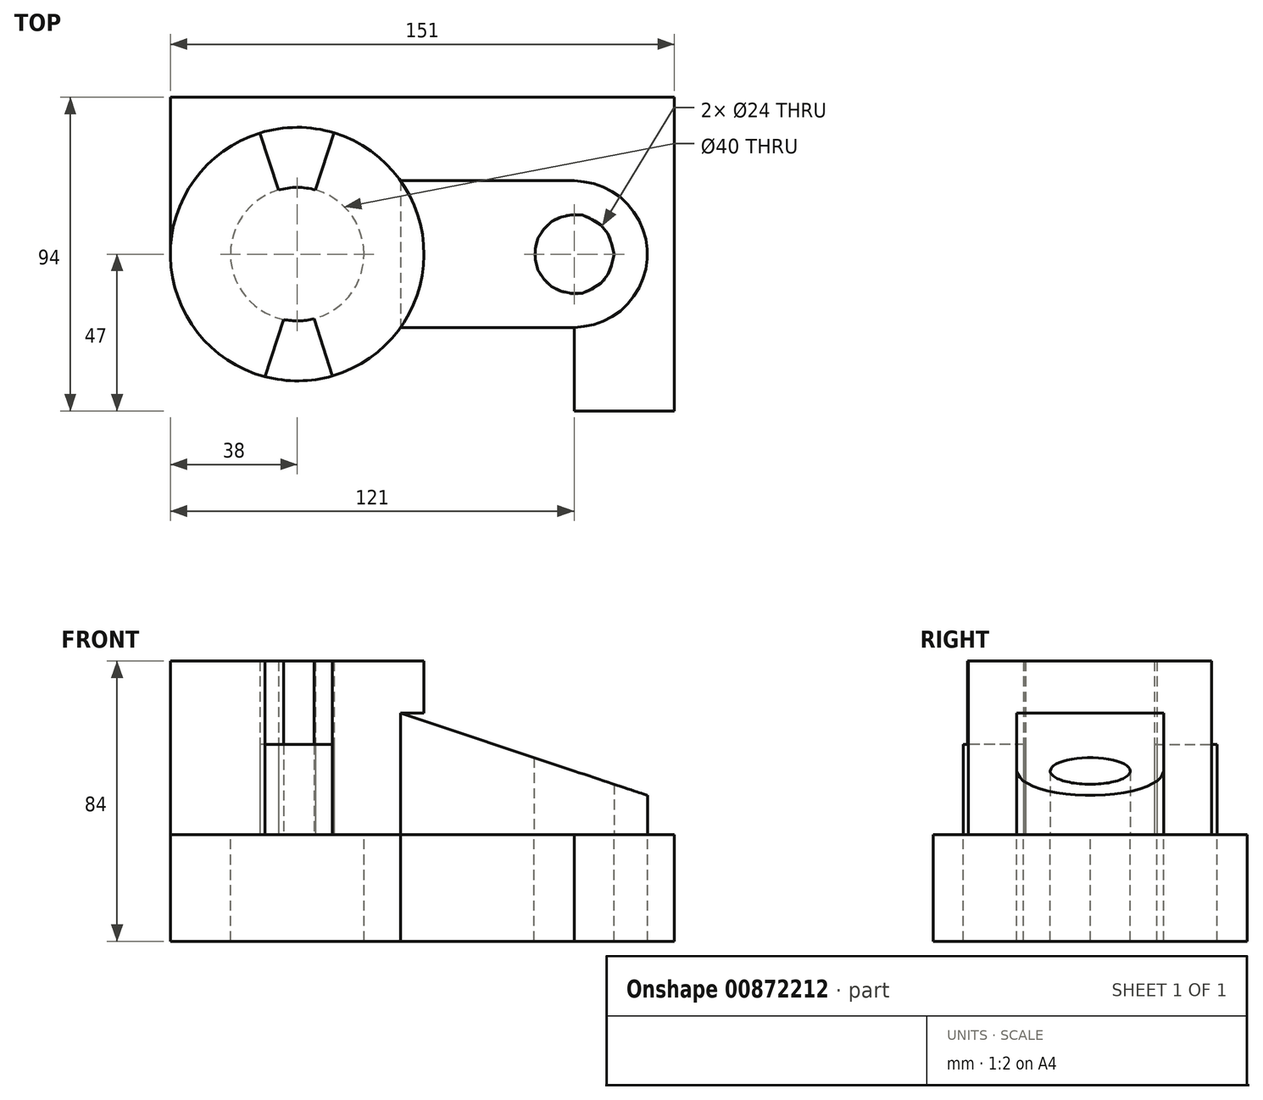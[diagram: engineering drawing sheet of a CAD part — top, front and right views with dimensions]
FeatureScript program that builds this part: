
annotation { "Feature Type Name" : "Feature", "Feature Type Description" : "" }
export const myFeature = defineFeature(function(context is Context, id is Id, definition is map)
    precondition{}
    {
        {
            var Q0;
            Q0=qCreatedBy(makeId("Top.planeOp"),FACE);
            var sketch = newSketch(context, id + "F0", { "sketchPlane" : qUnion([Q0])});
            skLineSegment(sketch, "E0.bottom", {"start": v(-56.5, 47) * mm, "end": v(56.5, 47) * mm});
            skLineSegment(sketch, "E0.top", {"start": v(-56.5, -47) * mm, "end": v(56.5, -47) * mm});
            skLineSegment(sketch, "E0.right", {"start": v(56.5, 47) * mm, "end": v(56.5, -47) * mm});
            skPoint(sketch, "E0.middle", {"position": v(0, 0) * mm});
            skCircle(sketch, "E1", {"center": v(-56.5, 0) * mm, "radius": 38 * mm});
            skLineSegment(sketch, "E2", {"start": v(-94.5, -47) * mm, "end": v(-56.5, -47) * mm});
            skLineSegment(sketch, "E3", {"start": v(-94.5, 47) * mm, "end": v(-56.5, 47) * mm});
            skLineSegment(sketch, "E4", {"start": v(56.5, -47) * mm, "end": v(26.5, -47) * mm});
            skLineSegment(sketch, "E5", {"start": v(26.5, -47) * mm, "end": v(26.5, 47) * mm});
            skCircle(sketch, "E6", {"center": v(26.5, 0) * mm, "radius": 12 * mm});
            skArc(sketch, "E7", {"start": v(26.5, -22) * mm, "mid": v(48.5, 0) * mm, "end": v(26.5, 22) * mm});
            skLineSegment(sketch, "E8", {"start": v(26.5, 22) * mm, "end": v(-25.52, 22) * mm});
            skLineSegment(sketch, "E9", {"start": v(26.5, -22) * mm, "end": v(-25.52, -22) * mm});
            skCircle(sketch, "E10", {"center": v(-56.5, 0) * mm, "radius": 20 * mm});
            skLineSegment(sketch, "E11", {"start": v(-51.48, -19.36) * mm, "end": v(-45.91, -36.5) * mm});
            skLineSegment(sketch, "E12", {"start": v(-56.5, 0) * mm, "end": v(-56.5, 38) * mm});
            skLineSegment(sketch, "E13", {"start": v(-56.5, 0) * mm, "end": v(-56.5, -38) * mm});
            skLineSegment(sketch, "E14", {"start": v(-51, 19.23) * mm, "end": v(-45.43, 36.35) * mm});
            skLineSegment(sketch, "E15", {"start": v(-62.12, 19.2) * mm, "end": v(-67.69, 36.32) * mm});
            skPoint(sketch, "E16.startSnap0", {"position": v(-56.5, -19) * mm});
            skLineSegment(sketch, "E17", {"start": v(-60.62, -19.57) * mm, "end": v(-66.2, -36.74) * mm});
            skLineSegment(sketch, "E18", {"start": v(-94.5, -47) * mm, "end": v(-94.5, 47) * mm});
            skSolve(sketch);
        }
        {
            var Q0;
            {var subQ0=sQuery(id+"F0.wireOp",EDGE,"E15");Q0=makeQuery(id+"F0.imprint","IMPRINT",FACE,{"disambiguationData":[TD([[makeQuery(id+"F0.imprint","IMPRINT",EDGE,{"derivedFrom":subQ0}),1.0]])]});}
            var Q1;
            {var subQ0=sQuery(id+"F0.wireOp",EDGE,"E11");Q1=makeQuery(id+"F0.imprint","IMPRINT",FACE,{"disambiguationData":[TD([[makeQuery(id+"F0.imprint","IMPRINT",EDGE,{"derivedFrom":subQ0}),1.0]])]});}
            var Q2;
            {var subQ3=sQuery(id+"F0.wireOp",EDGE,"E10");var subQ7=makeQuery(id+"F0.imprint","INTERSECT",VERTEX,{"derivedFrom":[subQ3,sQuery(id+"F0.wireOp",EDGE,"E14")]});Q2=makeQuery(id+"F0.imprint","IMPRINT",FACE,{"disambiguationData":[TD([[makeQuery(id+"F0.imprint","IMPRINT",EDGE,{"disambiguationData":[TD([[subQ7,-1.0]])],"derivedFrom":subQ3}),1.0]])]});}
            var Q3;
            {var subQ0=sQuery(id+"F0.wireOp",EDGE,"E10");var subQ7=makeQuery(id+"F0.imprint","INTERSECT",VERTEX,{"derivedFrom":[subQ0,sQuery(id+"F0.wireOp",EDGE,"E15")]});Q3=makeQuery(id+"F0.imprint","IMPRINT",FACE,{"disambiguationData":[TD([[makeQuery(id+"F0.imprint","IMPRINT",EDGE,{"disambiguationData":[TD([[subQ7,1.0]])],"derivedFrom":subQ0}),1.0]])]});}
            extrude(context, id + "F1", {"entities" : qUnion([Q0, Q1, Q2, Q3]), "depth" : (84 - 32) * mm, "offsetDistance" : 25 * mm});
        }
        {
            var Q0;
            {var subQ0=sQuery(id+"F0.wireOp",EDGE,"E11");Q0=makeQuery(id+"F0.imprint","IMPRINT",FACE,{"disambiguationData":[TD([[makeQuery(id+"F0.imprint","IMPRINT",EDGE,{"derivedFrom":subQ0}),-1.0]])]});}
            var Q1;
            {var subQ3=sQuery(id+"F0.wireOp",EDGE,"E17");Q1=makeQuery(id+"F0.imprint","IMPRINT",FACE,{"disambiguationData":[TD([[makeQuery(id+"F0.imprint","IMPRINT",EDGE,{"derivedFrom":subQ3}),1.0]])]});}
            var Q2;
            {var subQ3=sQuery(id+"F0.wireOp",EDGE,"E14");Q2=makeQuery(id+"F0.imprint","IMPRINT",FACE,{"disambiguationData":[TD([[makeQuery(id+"F0.imprint","IMPRINT",EDGE,{"derivedFrom":subQ3}),1.0]])]});}
            var Q3;
            {var subQ3=sQuery(id+"F0.wireOp",EDGE,"E15");Q3=makeQuery(id+"F0.imprint","IMPRINT",FACE,{"disambiguationData":[TD([[makeQuery(id+"F0.imprint","IMPRINT",EDGE,{"derivedFrom":subQ3}),-1.0]])]});}
            extrude(context, id + "F2", {"entities" : qUnion([Q0, Q1, Q2, Q3]), "depth" : (52 - 25) * mm, "offsetDistance" : 25 * mm});
        }
        {
            var Q0;
            {var subQ5=sQuery(id+"F0.wireOp",EDGE,"E3");Q0=makeQuery(id+"F0.imprint","IMPRINT",FACE,{"disambiguationData":[TD([[makeQuery(id+"F0.imprint","IMPRINT",EDGE,{"derivedFrom":subQ5}),-1.0]])]});}
            var Q1;
            {var subQ6=sQuery(id+"F0.wireOp",EDGE,"E0.top");Q1=makeQuery(id+"F0.imprint","IMPRINT",FACE,{"disambiguationData":[TD([[makeQuery(id+"F0.imprint","IMPRINT",EDGE,{"derivedFrom":subQ6}),1.0]])]});}
            extrude(context, id + "F3", {"entities" : qUnion([Q0, Q1]), "oppositeDirection" : true, "depth" : 32 * mm, "offsetDistance" : 25 * mm});
        }
        {
            var Q0;
            {var subQ1=sQuery(id+"F0.wireOp",EDGE,"E0.right");Q0=makeQuery(id+"F0.imprint","IMPRINT",FACE,{"disambiguationData":[TD([[makeQuery(id+"F0.imprint","IMPRINT",EDGE,{"derivedFrom":subQ1}),-1.0]])]});}
            extrude(context, id + "F4", {"entities" : qUnion([Q0]), "oppositeDirection" : true, "depth" : 32 * mm, "offsetDistance" : 25 * mm});
        }
        {
            var Q0;
            {var subQ4=sQuery(id+"F0.wireOp",EDGE,"E8");Q0=makeQuery(id+"F0.imprint","IMPRINT",FACE,{"disambiguationData":[TD([[makeQuery(id+"F0.imprint","IMPRINT",EDGE,{"derivedFrom":subQ4}),1.0]])]});}
            var Q1;
            {var subQ0=sQuery(id+"F0.wireOp",EDGE,"E7");Q1=makeQuery(id+"F0.imprint","IMPRINT",FACE,{"disambiguationData":[TD([[makeQuery(id+"F0.imprint","IMPRINT",EDGE,{"derivedFrom":subQ0}),1.0]])]});}
            extrude(context, id + "F5", {"entities" : qUnion([Q0, Q1]), "operationType" : NewBodyOperationType.ADD, "depth" : 12 * mm, "offsetDistance" : 25 * mm});
        }
        {
            var Q0;
            Q0=makeQuery(id+"F5.opExtrude","CAP_FACE",FACE,{"disambiguationData":[OSD([sQuery(id+"F0.wireOp",EDGE,"E1"),sQuery(id+"F0.wireOp",EDGE,"E6"),sQuery(id+"F0.wireOp",EDGE,"E7"),sQuery(id+"F0.wireOp",EDGE,"E8"),sQuery(id+"F0.wireOp",EDGE,"E9")])],"isStart":false});
            extrude(context, id + "F6", {"entities" : qUnion([Q0]), "operationType" : NewBodyOperationType.ADD, "depth" : 24.4 * mm, "offsetDistance" : 25 * mm});
        }
        {
            var Q0;
            {var subQ0=sQuery(id+"F0.wireOp",EDGE,"E9");Q0=makeQuery(id+"F6.boolean.opBoolean","MERGE",FACE,{"derivedFrom":[makeQuery(id+"F5.opExtrude","SWEPT_FACE",FACE,{"disambiguationData":[OSD([subQ0])]}),makeQuery(id+"F6.opExtrude","SWEPT_FACE",FACE,{"disambiguationData":[OSD([subQ0])]})]});}
            var sketch = newSketch(context, id + "F7", { "sketchPlane" : qUnion([Q0])});
            skLineSegment(sketch, "E19", {"start": v(48.5, 36.4) * mm, "end": v(48.5, 0) * mm});
            skLineSegment(sketch, "E20.0.0", {"start": v(-25.52, 0) * mm, "end": v(26.5, 0) * mm});
            skLineSegment(sketch, "E20.0.1", {"start": v(26.5, 0) * mm, "end": v(26.5, 36.4) * mm});
            skLineSegment(sketch, "E20.0.2", {"start": v(26.5, 36.4) * mm, "end": v(-25.52, 36.4) * mm});
            skLineSegment(sketch, "E20.0.3", {"start": v(-25.52, 36.4) * mm, "end": v(-25.52, 0) * mm});
            skLineSegment(sketch, "E21", {"start": v(-25.52, 36.4) * mm, "end": v(48.5, 11.72) * mm});
            skLineSegment(sketch, "E22", {"start": v(26.5, 36.4) * mm, "end": v(48.5, 36.4) * mm});
            skSolve(sketch);
        }
        {
            var Q0;
            {var subQ0=sQuery(id+"F7.wireOp",EDGE,"E20.0.2");Q0=makeQuery(id+"F7.imprint","IMPRINT",FACE,{"disambiguationData":[TD([[makeQuery(id+"F7.imprint","IMPRINT",EDGE,{"derivedFrom":subQ0}),1.0]])]});}
            var Q1;
            {var subQ0=sQuery(id+"F7.wireOp",EDGE,"E22");Q1=makeQuery(id+"F7.imprint","IMPRINT",FACE,{"disambiguationData":[TD([[makeQuery(id+"F7.imprint","IMPRINT",EDGE,{"derivedFrom":subQ0}),-1.0]])]});}
            extrude(context, id + "F8", {"entities" : qUnion([Q0, Q1]), "operationType" : NewBodyOperationType.REMOVE, "oppositeDirection" : true, "depth" : 74.5 * mm, "offsetDistance" : 25 * mm});
        }
        {
            var Q0;
            {var subQ0=sQuery(id+"F0.wireOp",EDGE,"E7");Q0=makeQuery(id+"F0.imprint","IMPRINT",FACE,{"disambiguationData":[TD([[makeQuery(id+"F0.imprint","IMPRINT",EDGE,{"derivedFrom":subQ0}),1.0]])]});}
            var Q1;
            {var subQ4=sQuery(id+"F0.wireOp",EDGE,"E8");Q1=makeQuery(id+"F0.imprint","IMPRINT",FACE,{"disambiguationData":[TD([[makeQuery(id+"F0.imprint","IMPRINT",EDGE,{"derivedFrom":subQ4}),1.0]])]});}
            var Q2;
            {var subQ3=sQuery(id+"F0.wireOp",EDGE,"E11");Q2=makeQuery(id+"F0.imprint","IMPRINT",FACE,{"disambiguationData":[TD([[makeQuery(id+"F0.imprint","IMPRINT",EDGE,{"derivedFrom":subQ3}),1.0]])]});}
            var Q3;
            {var subQ3=sQuery(id+"F0.wireOp",EDGE,"E14");Q3=makeQuery(id+"F0.imprint","IMPRINT",FACE,{"disambiguationData":[TD([[makeQuery(id+"F0.imprint","IMPRINT",EDGE,{"derivedFrom":subQ3}),1.0]])]});}
            var Q4;
            {var subQ3=sQuery(id+"F0.wireOp",EDGE,"E15");Q4=makeQuery(id+"F0.imprint","IMPRINT",FACE,{"disambiguationData":[TD([[makeQuery(id+"F0.imprint","IMPRINT",EDGE,{"derivedFrom":subQ3}),-1.0]])]});}
            var Q5;
            {var subQ0=sQuery(id+"F0.wireOp",EDGE,"E15");Q5=makeQuery(id+"F0.imprint","IMPRINT",FACE,{"disambiguationData":[TD([[makeQuery(id+"F0.imprint","IMPRINT",EDGE,{"derivedFrom":subQ0}),1.0]])]});}
            var Q6;
            {var subQ0=sQuery(id+"F0.wireOp",EDGE,"E11");Q6=makeQuery(id+"F0.imprint","IMPRINT",FACE,{"disambiguationData":[TD([[makeQuery(id+"F0.imprint","IMPRINT",EDGE,{"derivedFrom":subQ0}),-1.0]])]});}
            var Q7;
            {var subQ3=sQuery(id+"F0.wireOp",EDGE,"E17");Q7=makeQuery(id+"F0.imprint","IMPRINT",FACE,{"disambiguationData":[TD([[makeQuery(id+"F0.imprint","IMPRINT",EDGE,{"derivedFrom":subQ3}),1.0]])]});}
            extrude(context, id + "F9", {"entities" : qUnion([Q0, Q1, Q2, Q3, Q4, Q5, Q6, Q7]), "oppositeDirection" : true, "depth" : 32 * mm, "offsetDistance" : 25 * mm});
        }
    });
